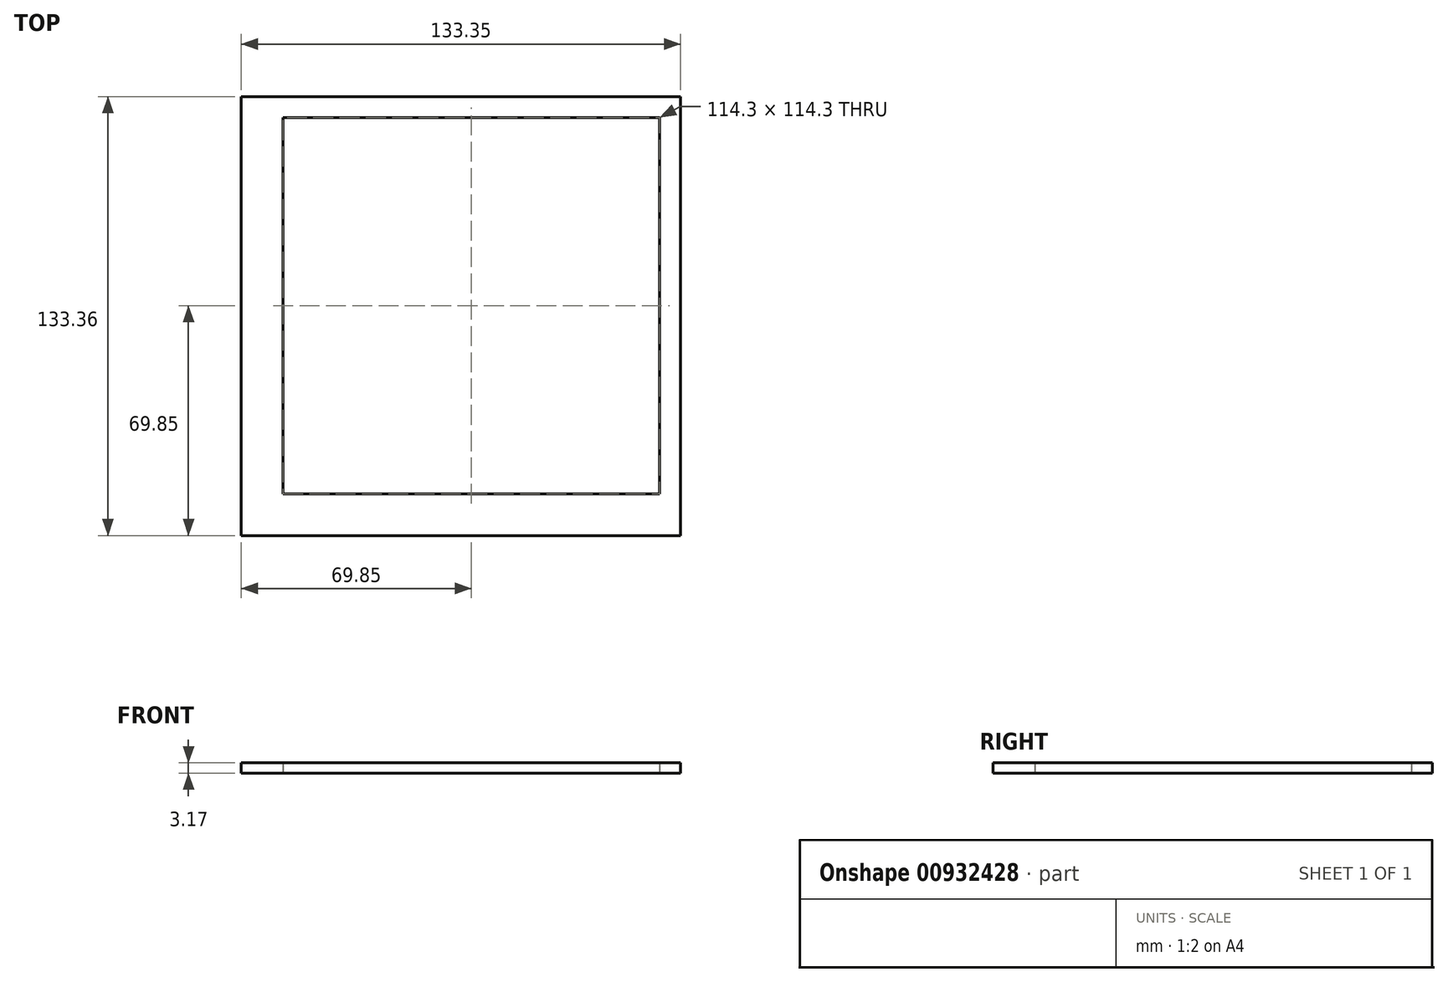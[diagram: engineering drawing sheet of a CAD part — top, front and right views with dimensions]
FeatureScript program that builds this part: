
annotation { "Feature Type Name" : "Feature", "Feature Type Description" : "" }
export const myFeature = defineFeature(function(context is Context, id is Id, definition is map)
    precondition{}
    {
        {
            var Q0;
            Q0=qCreatedBy(makeId("Top.planeOp"),FACE);
            var sketch = newSketch(context, id + "F0", { "sketchPlane" : qUnion([Q0])});
            skLineSegment(sketch, "E0.bottom", {"start": v(0, 0) * mm, "end": v(114.3, 0) * mm});
            skLineSegment(sketch, "E0.top", {"start": v(0, -114.3) * mm, "end": v(114.3, -114.3) * mm});
            skLineSegment(sketch, "E0.left", {"start": v(0, 0) * mm, "end": v(0, -114.3) * mm});
            skLineSegment(sketch, "E0.right", {"start": v(114.3, 0) * mm, "end": v(114.3, -114.3) * mm});
            skLineSegment(sketch, "E1", {"start": v(114.3, 6.35) * mm, "end": v(114.3, 0) * mm, "construction": true});
            skLineSegment(sketch, "E2", {"start": v(-12.7, 6.35) * mm, "end": v(-12.7, -127) * mm});
            skLineSegment(sketch, "E3", {"start": v(-12.7, -127) * mm, "end": v(124.56, -127) * mm});
            skLineSegment(sketch, "E4", {"start": v(124.56, -127) * mm, "end": v(120.65, -127) * mm});
            skLineSegment(sketch, "E5", {"start": v(120.65, 6.36) * mm, "end": v(120.65, -127) * mm});
            skLineSegment(sketch, "E6", {"start": v(114.3, 6.35) * mm, "end": v(120.65, 6.36) * mm});
            skLineSegment(sketch, "E7", {"start": v(-12.7, 6.35) * mm, "end": v(114.3, 6.35) * mm});
            skLineSegment(sketch, "E8", {"start": v(0, 0) * mm, "end": v(-12.7, 0) * mm, "construction": true});
            skLineSegment(sketch, "E9", {"start": v(114.3, 0) * mm, "end": v(120.65, 0) * mm, "construction": true});
            skLineSegment(sketch, "E10", {"start": v(0, -114.3) * mm, "end": v(0, -127) * mm, "construction": true});
            skSolve(sketch);
        }
        {
            var Q0;
            Q0 = qSketchRegion(id + "F0", true);
            extrude(context, id + "F1", {"entities" : qUnion([Q0]), "depth" : 3.17 * mm, "offsetDistance" : 25 * mm});
        }
    });
